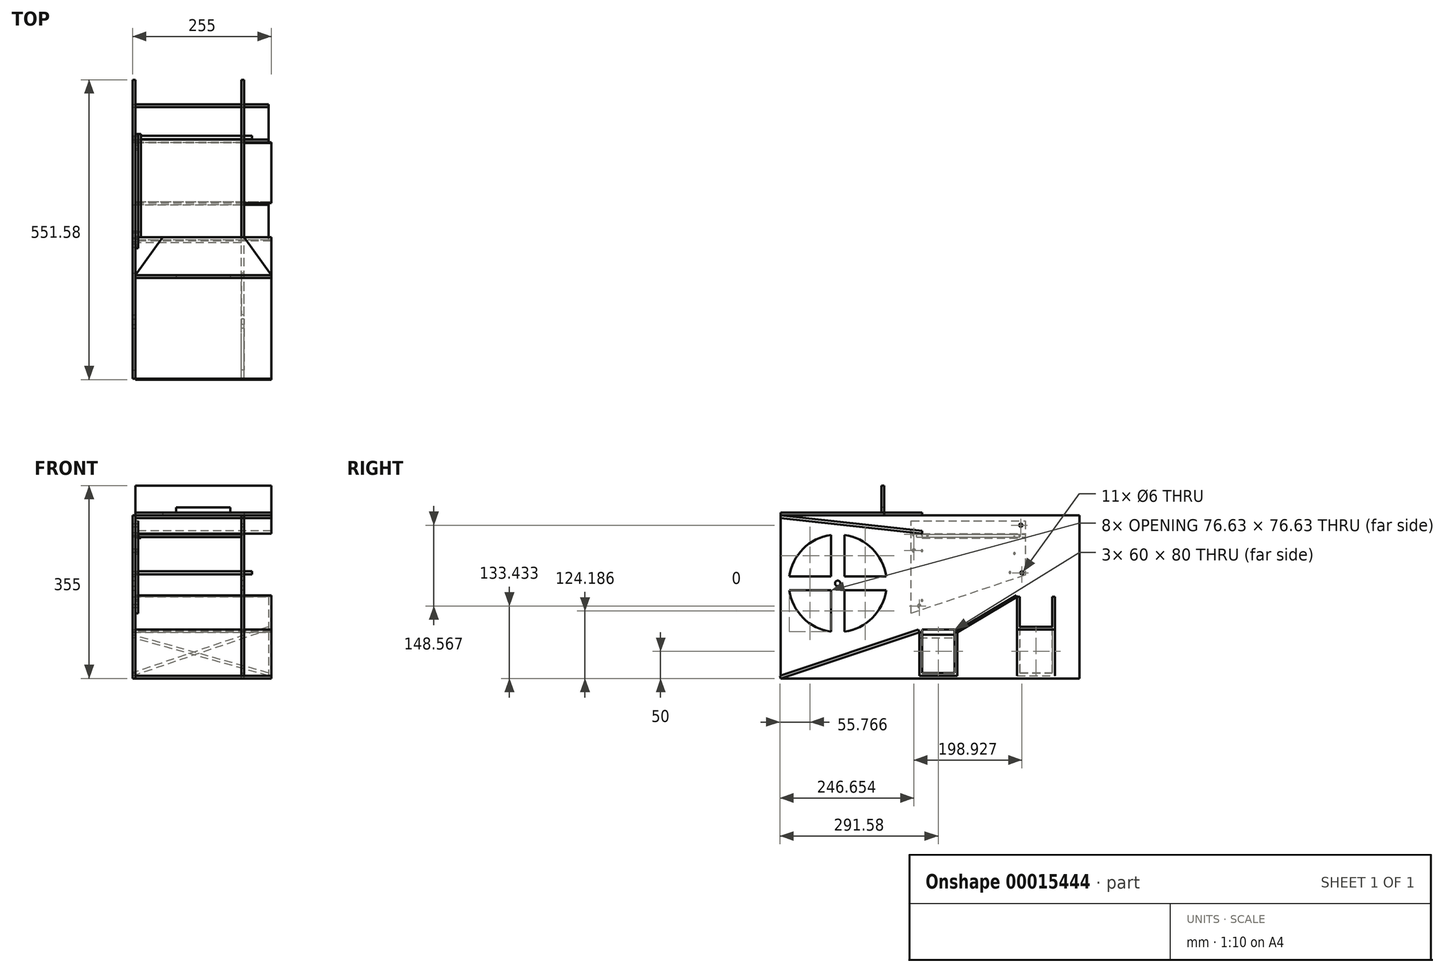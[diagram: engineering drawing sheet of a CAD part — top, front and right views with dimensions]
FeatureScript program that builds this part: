
annotation { "Feature Type Name" : "Feature", "Feature Type Description" : "" }
export const myFeature = defineFeature(function(context is Context, id is Id, definition is map)
    precondition{}
    {
        {
            var Q0;
            Q0=qCreatedBy(makeId("Right.planeOp"),FACE);
            var sketch = newSketch(context, id + "F0", { "sketchPlane" : qUnion([Q0])});
            skLineSegment(sketch, "E0.bottom", {"start": v(0, 0) * mm, "end": v(550, 0) * mm});
            skLineSegment(sketch, "E0.top", {"start": v(0, 300) * mm, "end": v(550, 300) * mm});
            skLineSegment(sketch, "E0.left", {"start": v(0, 0) * mm, "end": v(0, 300) * mm});
            skLineSegment(sketch, "E0.right", {"start": v(550, 0) * mm, "end": v(550, 300) * mm});
            skSolve(sketch);
        }
        {
            var Q0;
            Q0 = qSketchRegion(id + "F0", true);
            extrude(context, id + "F1", {"entities" : qUnion([Q0]), "depth" : 5 * mm});
        }
        {
            var Q0;
            Q0=makeQuery(id+"F1.opExtrude","CAP_FACE",FACE,{"disambiguationData":[OSD([sQuery(id+"F0.wireOp",EDGE,"E0.bottom"),sQuery(id+"F0.wireOp",EDGE,"E0.top"),sQuery(id+"F0.wireOp",EDGE,"E0.left"),sQuery(id+"F0.wireOp",EDGE,"E0.right")])],"isStart":false});
            var sketch = newSketch(context, id + "F2", { "sketchPlane" : qUnion([Q0])});
            skCircle(sketch, "E1", {"center": v(105, 175) * mm, "radius": 90 * mm});
            skLineSegment(sketch, "E2", {"start": v(52.33, 330.04) * mm, "end": v(82.37, 300) * mm});
            skLineSegment(sketch, "E3", {"start": v(82.37, 300) * mm, "end": v(199.7, 300) * mm});
            skLineSegment(sketch, "E4", {"start": v(199.7, 300) * mm, "end": v(229.74, 330.04) * mm});
            skLineSegment(sketch, "E5", {"start": v(82.37, 300) * mm, "end": v(250, 260) * mm});
            skLineSegment(sketch, "E6", {"start": v(250, 260) * mm, "end": v(440, 260) * mm});
            skLineSegment(sketch, "E7", {"start": v(440, 230) * mm, "end": v(250, 230) * mm});
            skLineSegment(sketch, "E8", {"start": v(440, 200) * mm, "end": v(256.2, 151.85) * mm});
            skLineSegment(sketch, "E9", {"start": v(263.12, 105.91) * mm, "end": v(44.4, 25.28) * mm});
            skLineSegment(sketch, "E10", {"start": v(440, 172.58) * mm, "end": v(440, 79.84) * mm});
            skLineSegment(sketch, "E11", {"start": v(440, 79.84) * mm, "end": v(500, 79.84) * mm});
            skLineSegment(sketch, "E12", {"start": v(500, 79.84) * mm, "end": v(500, 172.58) * mm});
            skLineSegment(sketch, "E13", {"start": v(323.12, 105.91) * mm, "end": v(323.12, 17.02) * mm});
            skLineSegment(sketch, "E14", {"start": v(323.12, 17.02) * mm, "end": v(263.12, 17.02) * mm});
            skLineSegment(sketch, "E15", {"start": v(263.12, 17.02) * mm, "end": v(263.12, 105.91) * mm});
            skLineSegment(sketch, "E16", {"start": v(323.12, 105.91) * mm, "end": v(440, 172.58) * mm});
            skSolve(sketch);
        }
        {
            var Q0;
            Q0=makeQuery(id+"F2.imprint","IMPRINT",FACE,{"disambiguationData":[TD([[makeQuery(id+"F2.imprint","IMPRINT",EDGE,{"derivedFrom":sQuery(id+"F2.wireOp",EDGE,"E1")}),-1.0]])]});
            var sketch = newSketch(context, id + "F3", { "sketchPlane" : qUnion([Q0])});
            skLineSegment(sketch, "E17", {"start": v(240, 290) * mm, "end": v(450, 290) * mm});
            skLineSegment(sketch, "E18", {"start": v(450, 290) * mm, "end": v(450, 190) * mm});
            skLineSegment(sketch, "E19", {"start": v(450, 190) * mm, "end": v(240, 120) * mm});
            skLineSegment(sketch, "E20", {"start": v(240, 120) * mm, "end": v(240, 290) * mm});
            skCircle(sketch, "E21", {"center": v(430, 260) * mm, "radius": 1.6 * mm});
            skCircle(sketch, "E22", {"center": v(430, 230) * mm, "radius": 1.6 * mm});
            skCircle(sketch, "E23", {"center": v(422.04, 195) * mm, "radius": 1.6 * mm});
            skCircle(sketch, "E24", {"center": v(260.07, 143.36) * mm, "radius": 1.6 * mm});
            skCircle(sketch, "E25", {"center": v(260.07, 235) * mm, "radius": 1.6 * mm});
            skCircle(sketch, "E26", {"center": v(260.07, 265) * mm, "radius": 1.6 * mm});
            skSolve(sketch);
        }
        {
            var Q0;
            Q0 = qSketchRegion(id + "F3", true);
            extrude(context, id + "F4", {"entities" : qUnion([Q0]), "depth" : 5 * mm});
        }
        {
            var Q0;
            Q0=makeQuery(id+"F4.opExtrude","CAP_FACE",FACE,{"disambiguationData":[OSD([sQuery(id+"F3.wireOp",EDGE,"E17"),sQuery(id+"F3.wireOp",EDGE,"E18"),sQuery(id+"F3.wireOp",EDGE,"E19"),sQuery(id+"F3.wireOp",EDGE,"E20")])],"isStart":false});
            var sketch = newSketch(context, id + "F5", { "sketchPlane" : qUnion([Q0])});
            skLineSegment(sketch, "E27.0", {"start": v(250, 260) * mm, "end": v(440, 260) * mm});
            skLineSegment(sketch, "E28", {"start": v(250, 260) * mm, "end": v(250, 265) * mm});
            skLineSegment(sketch, "E29", {"start": v(250, 265) * mm, "end": v(440, 265) * mm});
            skLineSegment(sketch, "E30", {"start": v(440, 265) * mm, "end": v(440, 260) * mm});
            skSolve(sketch);
        }
        {
            var Q0;
            Q0 = qSketchRegion(id + "F5", true);
            extrude(context, id + "F6", {"entities" : qUnion([Q0]), "depth" : 190 * mm});
        }
        {
            var Q0;
            Q0=makeQuery(id+"F2.imprint","IMPRINT",FACE,{"disambiguationData":[TD([[makeQuery(id+"F2.imprint","IMPRINT",EDGE,{"derivedFrom":sQuery(id+"F2.wireOp",EDGE,"E1")}),-1.0]])]});
            var sketch = newSketch(context, id + "F7", { "sketchPlane" : qUnion([Q0])});
            skArc(sketch, "E31.0", {"start": v(117.5, 85.87) * mm, "mid": v(168.64, 111.36) * mm, "end": v(194.13, 162.5) * mm});
            skLineSegment(sketch, "E32.rect.bottom", {"start": v(117.5, 85.87) * mm, "end": v(92.5, 85.87) * mm, "construction": true});
            skLineSegment(sketch, "E32.rect.top", {"start": v(117.5, 264.13) * mm, "end": v(92.5, 264.13) * mm, "construction": true});
            skLineSegment(sketch, "E32.rect.left", {"start": v(117.5, 85.87) * mm, "end": v(117.5, 162.5) * mm});
            skLineSegment(sketch, "E32.rect.right", {"start": v(92.5, 85.87) * mm, "end": v(92.5, 162.5) * mm});
            skLineSegment(sketch, "E33.rect.bottom", {"start": v(15.87, 187.5) * mm, "end": v(92.5, 187.5) * mm});
            skLineSegment(sketch, "E33.rect.top", {"start": v(15.87, 162.5) * mm, "end": v(92.5, 162.5) * mm});
            skLineSegment(sketch, "E33.rect.left", {"start": v(15.87, 187.5) * mm, "end": v(15.87, 162.5) * mm, "construction": true});
            skLineSegment(sketch, "E33.rect.right", {"start": v(194.13, 187.5) * mm, "end": v(194.13, 162.5) * mm, "construction": true});
            skLineSegment(sketch, "E34.trimOffspring", {"start": v(92.5, 187.5) * mm, "end": v(92.5, 264.13) * mm});
            skLineSegment(sketch, "E35.trimOffspring", {"start": v(117.5, 187.5) * mm, "end": v(194.13, 187.5) * mm});
            skLineSegment(sketch, "E36.trimOffspring", {"start": v(117.5, 187.5) * mm, "end": v(117.5, 264.13) * mm});
            skLineSegment(sketch, "E37.trimOffspring", {"start": v(117.5, 162.5) * mm, "end": v(194.13, 162.5) * mm});
            skArc(sketch, "E38.trimOffspring", {"start": v(194.13, 187.5) * mm, "mid": v(168.64, 238.64) * mm, "end": v(117.5, 264.13) * mm});
            skArc(sketch, "E39.trimOffspring", {"start": v(92.5, 264.13) * mm, "mid": v(41.36, 238.64) * mm, "end": v(15.87, 187.5) * mm});
            skArc(sketch, "E40.trimOffspring", {"start": v(15.87, 162.5) * mm, "mid": v(41.36, 111.36) * mm, "end": v(92.5, 85.87) * mm});
            skCircle(sketch, "E41", {"center": v(105, 175) * mm, "radius": 5 * mm});
            skSolve(sketch);
        }
        {
            var Q0;
            Q0 = qSketchRegion(id + "F7", true);
            extrude(context, id + "F8", {"entities" : qUnion([Q0]), "operationType" : NewBodyOperationType.REMOVE, "endBound" : BoundingType.THROUGH_ALL, "oppositeDirection" : true, "depth" : 25 * mm});
        }
        {
            var Q0;
            Q0=makeQuery(id+"F4.opExtrude","SWEPT_FACE",FACE,{"disambiguationData":[OSD([sQuery(id+"F3.wireOp",EDGE,"E18")])]});
            var sketch = newSketch(context, id + "F9", { "sketchPlane" : qUnion([Q0])});
            skPoint(sketch, "E42.0", {"position": v(-10, 260) * mm});
            skLineSegment(sketch, "E43", {"start": v(-10, 260) * mm, "end": v(-10, 266.5) * mm});
            skLineSegment(sketch, "E44", {"start": v(-10, 266.5) * mm, "end": v(-15, 266.5) * mm});
            skLineSegment(sketch, "E45", {"start": v(-15, 266.5) * mm, "end": v(-15, 265) * mm});
            skLineSegment(sketch, "E46", {"start": v(-15, 265) * mm, "end": v(-11.5, 265) * mm});
            skLineSegment(sketch, "E47", {"start": v(-11.5, 265) * mm, "end": v(-11.5, 260) * mm});
            skLineSegment(sketch, "E48", {"start": v(-11.5, 260) * mm, "end": v(-15, 260) * mm});
            skLineSegment(sketch, "E49", {"start": v(-15, 260) * mm, "end": v(-15, 258.5) * mm});
            skLineSegment(sketch, "E50", {"start": v(-15, 258.5) * mm, "end": v(-10, 258.5) * mm});
            skLineSegment(sketch, "E51", {"start": v(-10, 258.5) * mm, "end": v(-10, 260) * mm});
            skSolve(sketch);
        }
        {
            var Q0;
            Q0 = qSketchRegion(id + "F9", true);
            var Q1;
            Q1=makeQuery(id+"F4.opExtrude","SWEPT_FACE",FACE,{"disambiguationData":[OSD([sQuery(id+"F3.wireOp",EDGE,"E20")])]});
            extrude(context, id + "F10", {"entities" : qUnion([Q0]), "oppositeDirection" : true, "endBoundEntityFace" : qUnion([Q1]), "depth" : 190 * mm});
        }
        {
            var Q0;
            Q0=makeQuery(id+"F6.opExtrude","CAP_FACE",FACE,{"disambiguationData":[OSD([sQuery(id+"F5.wireOp",EDGE,"E27.0"),sQuery(id+"F5.wireOp",EDGE,"E28"),sQuery(id+"F5.wireOp",EDGE,"E29"),sQuery(id+"F5.wireOp",EDGE,"E30")])],"isStart":false});
            var sketch = newSketch(context, id + "F11", { "sketchPlane" : qUnion([Q0])});
            skLineSegment(sketch, "E52.0", {"start": v(0, 300) * mm, "end": v(550, 300) * mm});
            skLineSegment(sketch, "E52.1", {"start": v(0, 0) * mm, "end": v(0, 300) * mm});
            skArc(sketch, "E52.2", {"start": v(92.5, 264.13) * mm, "mid": v(41.36, 238.64) * mm, "end": v(15.87, 187.5) * mm});
            skLineSegment(sketch, "E52.3", {"start": v(0, 0) * mm, "end": v(550, 0) * mm});
            skLineSegment(sketch, "E52.4", {"start": v(550, 0) * mm, "end": v(550, 300) * mm});
            skLineSegment(sketch, "E53.0", {"start": v(117.5, 187.5) * mm, "end": v(117.5, 264.13) * mm});
            skLineSegment(sketch, "E53.1", {"start": v(117.5, 187.5) * mm, "end": v(194.13, 187.5) * mm});
            skLineSegment(sketch, "E53.2", {"start": v(117.5, 162.5) * mm, "end": v(194.13, 162.5) * mm});
            skLineSegment(sketch, "E53.3", {"start": v(117.5, 85.87) * mm, "end": v(117.5, 162.5) * mm});
            skLineSegment(sketch, "E53.4", {"start": v(92.5, 85.87) * mm, "end": v(92.5, 162.5) * mm});
            skLineSegment(sketch, "E53.5", {"start": v(15.87, 162.5) * mm, "end": v(92.5, 162.5) * mm});
            skLineSegment(sketch, "E53.6", {"start": v(15.87, 187.5) * mm, "end": v(92.5, 187.5) * mm});
            skLineSegment(sketch, "E53.7", {"start": v(92.5, 187.5) * mm, "end": v(92.5, 264.13) * mm});
            skCircle(sketch, "E53.8", {"center": v(105, 175) * mm, "radius": 5 * mm});
            skArc(sketch, "E54.trimOffspring", {"start": v(194.13, 187.5) * mm, "mid": v(168.64, 238.64) * mm, "end": v(117.5, 264.13) * mm});
            skArc(sketch, "E55.trimOffspring", {"start": v(15.87, 162.5) * mm, "mid": v(41.36, 111.36) * mm, "end": v(92.5, 85.87) * mm});
            skArc(sketch, "E56.trimOffspring", {"start": v(117.5, 85.87) * mm, "mid": v(168.64, 111.36) * mm, "end": v(194.13, 162.5) * mm});
            skSolve(sketch);
        }
        {
            var Q0;
            Q0 = qSketchRegion(id + "F11", true);
            extrude(context, id + "F12", {"entities" : qUnion([Q0]), "depth" : 5 * mm});
        }
        {
            var Q0;
            Q0=makeQuery(id+"F2.imprint","IMPRINT",FACE,{"disambiguationData":[TD([[makeQuery(id+"F2.imprint","IMPRINT",EDGE,{"derivedFrom":sQuery(id+"F2.wireOp",EDGE,"E1")}),-1.0]])]});
            var sketch = newSketch(context, id + "F13", { "sketchPlane" : qUnion([Q0])});
            skLineSegment(sketch, "E57.bottom", {"start": v(440, 10) * mm, "end": v(500, 10) * mm});
            skLineSegment(sketch, "E57.top", {"start": v(440, 90) * mm, "end": v(500, 90) * mm});
            skLineSegment(sketch, "E57.left", {"start": v(440, 10) * mm, "end": v(440, 90) * mm});
            skLineSegment(sketch, "E57.right", {"start": v(500, 10) * mm, "end": v(500, 90) * mm});
            skLineSegment(sketch, "E58.0", {"start": v(550, 0) * mm, "end": v(550, 300) * mm, "construction": true});
            skSolve(sketch);
        }
        {
            var Q0;
            Q0 = qSketchRegion(id + "F13", true);
            extrude(context, id + "F14", {"entities" : qUnion([Q0]), "operationType" : NewBodyOperationType.REMOVE, "endBound" : BoundingType.THROUGH_ALL, "oppositeDirection" : true, "depth" : 25 * mm});
        }
        {
            var Q0;
            Q0=makeQuery(id+"F12.opExtrude","CAP_FACE",FACE,{"disambiguationData":[OSD([sQuery(id+"F11.wireOp",EDGE,"E52.0"),sQuery(id+"F11.wireOp",EDGE,"E52.1"),sQuery(id+"F11.wireOp",EDGE,"E52.2"),sQuery(id+"F11.wireOp",EDGE,"E52.3"),sQuery(id+"F11.wireOp",EDGE,"E52.4"),sQuery(id+"F11.wireOp",EDGE,"E53.0"),sQuery(id+"F11.wireOp",EDGE,"E53.1"),sQuery(id+"F11.wireOp",EDGE,"E53.2"),sQuery(id+"F11.wireOp",EDGE,"E53.3"),sQuery(id+"F11.wireOp",EDGE,"E53.4"),sQuery(id+"F11.wireOp",EDGE,"E53.5"),sQuery(id+"F11.wireOp",EDGE,"E53.6"),sQuery(id+"F11.wireOp",EDGE,"E53.7"),sQuery(id+"F11.wireOp",EDGE,"E53.8"),sQuery(id+"F11.wireOp",EDGE,"E54.trimOffspring"),sQuery(id+"F11.wireOp",EDGE,"E55.trimOffspring"),sQuery(id+"F11.wireOp",EDGE,"E56.trimOffspring")])],"isStart":false});
            var sketch = newSketch(context, id + "F15", { "sketchPlane" : qUnion([Q0])});
            skLineSegment(sketch, "E59.bottom", {"start": v(260, 10) * mm, "end": v(320, 10) * mm});
            skLineSegment(sketch, "E59.top", {"start": v(260, 90) * mm, "end": v(320, 90) * mm});
            skLineSegment(sketch, "E59.left", {"start": v(260, 10) * mm, "end": v(260, 90) * mm});
            skLineSegment(sketch, "E59.right", {"start": v(320, 10) * mm, "end": v(320, 90) * mm});
            skSolve(sketch);
        }
        {
            var Q0;
            Q0 = qSketchRegion(id + "F15", true);
            extrude(context, id + "F16", {"entities" : qUnion([Q0]), "operationType" : NewBodyOperationType.REMOVE, "endBound" : BoundingType.THROUGH_ALL, "oppositeDirection" : true, "depth" : 25 * mm});
        }
        {
            var Q0;
            Q0=qCreatedBy(makeId("Right.planeOp"),FACE);
            var sketch = newSketch(context, id + "F17", { "sketchPlane" : qUnion([Q0])});
            skLineSegment(sketch, "E60.0", {"start": v(440, 10) * mm, "end": v(440, 90) * mm, "construction": true});
            skLineSegment(sketch, "E61.0", {"start": v(500, 10) * mm, "end": v(500, 90) * mm, "construction": true});
            skLineSegment(sketch, "E62.0", {"start": v(440, 10) * mm, "end": v(500, 10) * mm, "construction": true});
            skLineSegment(sketch, "E63.0", {"start": v(435, 5) * mm, "end": v(435, 150) * mm});
            skLineSegment(sketch, "E63.2", {"start": v(435, 5) * mm, "end": v(505, 5) * mm});
            skLineSegment(sketch, "E63.4", {"start": v(505, 150) * mm, "end": v(505, 5) * mm});
            skLineSegment(sketch, "E64", {"start": v(435, 150) * mm, "end": v(505, 150) * mm});
            skSolve(sketch);
        }
        {
            var Q0;
            Q0=qCreatedBy(makeId("Right.planeOp"),FACE);
            cPlane(context, id + "F18", {"entities" : qUnion([Q0]), "cplaneType" : CPlaneType.OFFSET, "offset" : 250 * mm, "width" : 150 * mm, "height" : 150 * mm});
        }
        {
            var Q0;
            Q0=qCreatedBy(id+"F18.planeOp",FACE);
            var sketch = newSketch(context, id + "F19", { "sketchPlane" : qUnion([Q0])});
            skLineSegment(sketch, "E65.0.3", {"start": v(505, 150) * mm, "end": v(435, 150) * mm});
            skLineSegment(sketch, "E66", {"start": v(435, 150) * mm, "end": v(435, 90) * mm});
            skLineSegment(sketch, "E67", {"start": v(435, 90) * mm, "end": v(505, 90) * mm});
            skLineSegment(sketch, "E68", {"start": v(505, 90) * mm, "end": v(505, 150) * mm});
            skSolve(sketch);
        }
        {
            var Q1;
            Q1 = qSketchRegion(id + "F17", true);
            var Q2;
            Q2 = qSketchRegion(id + "F19", true);
            loft(context, id + "F20", {"sheetProfilesArray" : [{ "sheetProfileEntities" : qUnion([Q1]) }, { "sheetProfileEntities" : qUnion([Q2]) }]});
        }
        {
            var Q0;
            Q0=makeQuery(id+"F20.opLoft","SWEPT_FACE",FACE,{"disambiguationData":[OSD([sQuery(id+"F17.wireOp",EDGE,"E63.0"),sQuery(id+"F17.wireOp",EDGE,"E63.4"),sQuery(id+"F17.wireOp",EDGE,"E64"),sQuery(id+"F19.wireOp",EDGE,"E65.0.3"),sQuery(id+"F19.wireOp",EDGE,"E66"),sQuery(id+"F19.wireOp",EDGE,"E68")])]});
            var Q1;
            Q1=makeQuery(id+"F20.opLoft","CAP_FACE",FACE,{"disambiguationData":[OSD([makeQuery(id+"F19.imprint","IMPRINT",FACE,{"disambiguationData":[TD([[makeQuery(id+"F19.imprint","IMPRINT",EDGE,{"derivedFrom":sQuery(id+"F19.wireOp",EDGE,"E65.0.3")}),1.0]])]})])],"isStart":true});
            var Q2;
            Q2=makeQuery(id+"F20.opLoft","CAP_FACE",FACE,{"disambiguationData":[OSD([makeQuery(id+"F17.imprint","IMPRINT",FACE,{"disambiguationData":[TD([[makeQuery(id+"F17.imprint","IMPRINT",EDGE,{"derivedFrom":sQuery(id+"F17.wireOp",EDGE,"E63.0")}),-1.0]])]})])],"isStart":true});
            shell(context, id + "F21", {"entities" : qUnion([Q0, Q1, Q2]), "thickness" : 5 * mm});
        }
        {
            var Q0;
            Q0=qCreatedBy(id+"F18.planeOp",FACE);
            var sketch = newSketch(context, id + "F22", { "sketchPlane" : qUnion([Q0])});
            skLineSegment(sketch, "E69.bottom", {"start": v(255, 85) * mm, "end": v(325, 85) * mm});
            skLineSegment(sketch, "E69.top", {"start": v(255, 5) * mm, "end": v(325, 5) * mm});
            skLineSegment(sketch, "E69.left", {"start": v(255, 85) * mm, "end": v(255, 5) * mm});
            skLineSegment(sketch, "E69.right", {"start": v(325, 85) * mm, "end": v(325, 5) * mm});
            skPoint(sketch, "E70.0", {"position": v(260, 10) * mm});
            skPoint(sketch, "E70.1", {"position": v(320, 10) * mm});
            skSolve(sketch);
        }
        {
            var Q0;
            Q0=qCreatedBy(makeId("Right.planeOp"),FACE);
            var sketch = newSketch(context, id + "F23", { "sketchPlane" : qUnion([Q0])});
            skPoint(sketch, "E71.0", {"position": v(255, 85) * mm});
            skLineSegment(sketch, "E71.1", {"start": v(255, 85) * mm, "end": v(325, 85) * mm});
            skPoint(sketch, "E71.2", {"position": v(325, 85) * mm});
            skLineSegment(sketch, "E72", {"start": v(255, 85) * mm, "end": v(255, 75) * mm});
            skLineSegment(sketch, "E73", {"start": v(255, 75) * mm, "end": v(325, 75) * mm});
            skLineSegment(sketch, "E74", {"start": v(325, 75) * mm, "end": v(325, 85) * mm});
            skSolve(sketch);
        }
        {
            var Q0;
            Q0 = qSketchRegion(id + "F22", true);
            var Q1;
            Q1 = qSketchRegion(id + "F23", true);
            loft(context, id + "F24", {"sheetProfilesArray" : [{ "sheetProfileEntities" : qUnion([Q0]) }, { "sheetProfileEntities" : qUnion([Q1]) }]});
        }
        {
            var Q0;
            Q0=makeQuery(id+"F24.opLoft","SWEPT_FACE",FACE,{"disambiguationData":[OSD([sQuery(id+"F22.wireOp",EDGE,"E69.bottom"),sQuery(id+"F22.wireOp",EDGE,"E69.left"),sQuery(id+"F22.wireOp",EDGE,"E69.right"),sQuery(id+"F23.wireOp",EDGE,"E71.1"),sQuery(id+"F23.wireOp",EDGE,"a4f3d3e9-b016-48f9-8659-834d968ab62a"),sQuery(id+"F23.wireOp",EDGE,"384a152d-da16-4bd5-ac45-8ecb57b86d58")])]});
            var Q1;
            Q1=makeQuery(id+"F24.opLoft","CAP_FACE",FACE,{"disambiguationData":[OSD([makeQuery(id+"F22.imprint","IMPRINT",FACE,{"disambiguationData":[TD([[makeQuery(id+"F22.imprint","IMPRINT",EDGE,{"derivedFrom":sQuery(id+"F22.wireOp",EDGE,"E69.bottom")}),-1.0]])]})])],"isStart":true});
            var Q2;
            Q2=makeQuery(id+"F24.opLoft","CAP_FACE",FACE,{"disambiguationData":[OSD([makeQuery(id+"F23.imprint","IMPRINT",FACE,{"disambiguationData":[TD([[makeQuery(id+"F23.imprint","IMPRINT",EDGE,{"derivedFrom":sQuery(id+"F23.wireOp",EDGE,"E71.1")}),-1.0]])]})])],"isStart":true});
            shell(context, id + "F25", {"entities" : qUnion([Q0, Q1, Q2]), "thickness" : 5 * mm});
        }
        {
            var Q0;
            Q0=makeQuery(id+"F1.opExtrude","CAP_FACE",FACE,{"disambiguationData":[OSD([sQuery(id+"F0.wireOp",EDGE,"E0.bottom"),sQuery(id+"F0.wireOp",EDGE,"E0.top"),sQuery(id+"F0.wireOp",EDGE,"E0.left"),sQuery(id+"F0.wireOp",EDGE,"E0.right")])],"isStart":false});
            var sketch = newSketch(context, id + "F26", { "sketchPlane" : qUnion([Q0])});
            skPoint(sketch, "E75.0", {"position": v(435, 150) * mm});
            skPoint(sketch, "E76.0", {"position": v(325, 85) * mm});
            skLineSegment(sketch, "E77", {"start": v(325, 85) * mm, "end": v(435, 150) * mm});
            skLineSegment(sketch, "E78", {"start": v(435, 150) * mm, "end": v(433.47, 152.58) * mm});
            skLineSegment(sketch, "E79", {"start": v(433.47, 152.58) * mm, "end": v(323.47, 87.58) * mm});
            skLineSegment(sketch, "E80", {"start": v(323.47, 87.58) * mm, "end": v(325, 85) * mm});
            skSolve(sketch);
        }
        {
            var Q0;
            Q0 = qSketchRegion(id + "F26", true);
            extrude(context, id + "F27", {"entities" : qUnion([Q0]), "depth" : 250 * mm});
        }
        {
            var Q0;
            Q0=makeQuery(id+"F10.opExtrude","SWEPT_FACE",FACE,{"disambiguationData":[OSD([sQuery(id+"F9.wireOp",EDGE,"E47")])]});
            var sketch = newSketch(context, id + "F28", { "sketchPlane" : qUnion([Q0])});
            skCircle(sketch, "E81", {"center": v(440, 262.5) * mm, "radius": 1.6 * mm});
            skCircle(sketch, "E82", {"center": v(270, 262.5) * mm, "radius": 1.6 * mm});
            skLineSegment(sketch, "E83.0", {"start": v(450, 265) * mm, "end": v(450, 260) * mm, "construction": true});
            skPoint(sketch, "E84", {"position": v(450, 262.5) * mm});
            skSolve(sketch);
        }
        {
            var Q0;
            Q0 = qSketchRegion(id + "F28", true);
            extrude(context, id + "F29", {"entities" : qUnion([Q0]), "operationType" : NewBodyOperationType.REMOVE, "endBound" : BoundingType.THROUGH_ALL, "oppositeDirection" : true, "depth" : 25 * mm});
        }
        {
            var Q0;
            Q0=makeQuery(id+"F1.opExtrude","CAP_FACE",FACE,{"disambiguationData":[OSD([sQuery(id+"F0.wireOp",EDGE,"E0.bottom"),sQuery(id+"F0.wireOp",EDGE,"E0.top"),sQuery(id+"F0.wireOp",EDGE,"E0.left"),sQuery(id+"F0.wireOp",EDGE,"E0.right")])],"isStart":false});
            var sketch = newSketch(context, id + "F30", { "sketchPlane" : qUnion([Q0])});
            skPoint(sketch, "E85.0", {"position": v(260, 266.5) * mm});
            skLineSegment(sketch, "E86", {"start": v(260, 266.5) * mm, "end": v(0, 294.97) * mm});
            skLineSegment(sketch, "E87", {"start": v(0, 294.97) * mm, "end": v(0, 300) * mm});
            skLineSegment(sketch, "E88", {"start": v(0, 300) * mm, "end": v(260.54, 271.47) * mm});
            skLineSegment(sketch, "E89", {"start": v(260.54, 271.47) * mm, "end": v(260, 266.5) * mm});
            skSolve(sketch);
        }
        {
            var Q0;
            Q0 = qSketchRegion(id + "F30", true);
            extrude(context, id + "F31", {"entities" : qUnion([Q0]), "depth" : 250 * mm});
        }
        {
            var Q0;
            Q0=makeQuery(id+"F1.opExtrude","CAP_FACE",FACE,{"disambiguationData":[OSD([sQuery(id+"F0.wireOp",EDGE,"E0.bottom"),sQuery(id+"F0.wireOp",EDGE,"E0.top"),sQuery(id+"F0.wireOp",EDGE,"E0.left"),sQuery(id+"F0.wireOp",EDGE,"E0.right")])],"isStart":false});
            var sketch = newSketch(context, id + "F32", { "sketchPlane" : qUnion([Q0])});
            skLineSegment(sketch, "E90", {"start": v(0, 0) * mm, "end": v(255, 85) * mm});
            skLineSegment(sketch, "E91", {"start": v(255, 85) * mm, "end": v(253.42, 89.74) * mm});
            skLineSegment(sketch, "E92", {"start": v(253.42, 89.74) * mm, "end": v(-1.58, 4.74) * mm});
            skLineSegment(sketch, "E93", {"start": v(-1.58, 4.74) * mm, "end": v(0, 0) * mm});
            skPoint(sketch, "E94.0", {"position": v(255, 85) * mm});
            skSolve(sketch);
        }
        {
            var Q0;
            Q0 = qSketchRegion(id + "F32", true);
            extrude(context, id + "F33", {"entities" : qUnion([Q0]), "depth" : 250 * mm});
        }
        {
            var Q0;
            Q0=makeQuery(id+"F1.opExtrude","SWEPT_FACE",FACE,{"disambiguationData":[OSD([sQuery(id+"F0.wireOp",EDGE,"E0.top")])]});
            var sketch = newSketch(context, id + "F34", { "sketchPlane" : qUnion([Q0])});
            skLineSegment(sketch, "E95.0.0", {"start": v(5, 260.54) * mm, "end": v(5, 0) * mm, "construction": true});
            skLineSegment(sketch, "E95.0.1", {"start": v(5, 0) * mm, "end": v(255, 0) * mm});
            skLineSegment(sketch, "E95.0.2", {"start": v(255, 0) * mm, "end": v(255, 260.54) * mm, "construction": true});
            skLineSegment(sketch, "E95.0.3", {"start": v(255, 260.54) * mm, "end": v(5, 260.54) * mm, "construction": true});
            skLineSegment(sketch, "E96", {"start": v(5, 0) * mm, "end": v(5, 190.54) * mm});
            skLineSegment(sketch, "E97", {"start": v(5, 190.54) * mm, "end": v(55, 260.54) * mm});
            skLineSegment(sketch, "E98", {"start": v(55, 260.54) * mm, "end": v(205, 260.54) * mm});
            skLineSegment(sketch, "E99", {"start": v(205, 260.54) * mm, "end": v(255, 190.54) * mm});
            skLineSegment(sketch, "E100", {"start": v(255, 190.54) * mm, "end": v(255, 0) * mm});
            skSolve(sketch);
        }
        {
            var Q0;
            Q0 = qSketchRegion(id + "F34", true);
            extrude(context, id + "F35", {"entities" : qUnion([Q0]), "depth" : 5 * mm});
        }
        {
            var Q0;
            Q0=makeQuery(id+"F35.opExtrude","CAP_FACE",FACE,{"disambiguationData":[OSD([sQuery(id+"F34.wireOp",EDGE,"E95.0.1"),sQuery(id+"F34.wireOp",EDGE,"E96"),sQuery(id+"F34.wireOp",EDGE,"E97"),sQuery(id+"F34.wireOp",EDGE,"E98"),sQuery(id+"F34.wireOp",EDGE,"E99"),sQuery(id+"F34.wireOp",EDGE,"E100")])],"isStart":false});
            var sketch = newSketch(context, id + "F36", { "sketchPlane" : qUnion([Q0])});
            skLineSegment(sketch, "E101.bottom", {"start": v(5, 190.54) * mm, "end": v(255, 190.54) * mm});
            skLineSegment(sketch, "E101.top", {"start": v(5, 185.54) * mm, "end": v(255, 185.54) * mm});
            skLineSegment(sketch, "E101.left", {"start": v(5, 190.54) * mm, "end": v(5, 185.54) * mm});
            skLineSegment(sketch, "E101.right", {"start": v(255, 190.54) * mm, "end": v(255, 185.54) * mm});
            skSolve(sketch);
        }
        {
            var Q0;
            Q0 = qSketchRegion(id + "F36", true);
            extrude(context, id + "F37", {"entities" : qUnion([Q0]), "depth" : 50 * mm});
        }
        {
            var Q0;
            Q0=makeQuery(id+"F37.opExtrude","SWEPT_FACE",FACE,{"disambiguationData":[OSD([sQuery(id+"F36.wireOp",EDGE,"E101.top")])]});
            var sketch = newSketch(context, id + "F38", { "sketchPlane" : qUnion([Q0])});
            skLineSegment(sketch, "E102.bottom", {"start": v(80, 305) * mm, "end": v(180, 305) * mm});
            skLineSegment(sketch, "E102.top", {"start": v(80, 315) * mm, "end": v(180, 315) * mm});
            skLineSegment(sketch, "E102.left", {"start": v(80, 305) * mm, "end": v(80, 315) * mm});
            skLineSegment(sketch, "E102.right", {"start": v(180, 305) * mm, "end": v(180, 315) * mm});
            skPoint(sketch, "E103", {"position": v(130, 305) * mm});
            skSolve(sketch);
        }
        {
            var Q0;
            Q0 = qSketchRegion(id + "F38", true);
            extrude(context, id + "F39", {"entities" : qUnion([Q0]), "operationType" : NewBodyOperationType.REMOVE, "endBound" : BoundingType.THROUGH_ALL, "oppositeDirection" : true, "depth" : 25 * mm});
        }
        {
            var Q0;
            Q0=makeQuery(id+"F4.opExtrude","CAP_FACE",FACE,{"disambiguationData":[OSD([sQuery(id+"F3.wireOp",EDGE,"E17"),sQuery(id+"F3.wireOp",EDGE,"E18"),sQuery(id+"F3.wireOp",EDGE,"E19"),sQuery(id+"F3.wireOp",EDGE,"E20"),sQuery(id+"F3.wireOp",EDGE,"E21"),sQuery(id+"F3.wireOp",EDGE,"E22"),sQuery(id+"F3.wireOp",EDGE,"E23"),sQuery(id+"F3.wireOp",EDGE,"E24"),sQuery(id+"F3.wireOp",EDGE,"E25"),sQuery(id+"F3.wireOp",EDGE,"E26")])],"isStart":false});
            var sketch = newSketch(context, id + "F40", { "sketchPlane" : qUnion([Q0])});
            skCircle(sketch, "E104", {"center": v(442, 282) * mm, "radius": 3 * mm});
            skSolve(sketch);
        }
        {
            var Q0;
            Q0 = qSketchRegion(id + "F40", true);
            extrude(context, id + "F41", {"entities" : qUnion([Q0]), "operationType" : NewBodyOperationType.REMOVE, "endBound" : BoundingType.THROUGH_ALL, "oppositeDirection" : true, "depth" : 25 * mm, "hasSecondDirection" : true, "secondDirectionBound" : BoundingType.THROUGH_ALL, "secondDirectionOppositeDirection" : false, "secondDirectionDepth" : 25 * mm});
        }
        {
            var Q0;
            Q0=makeQuery(id+"F4.opExtrude","CAP_FACE",FACE,{"disambiguationData":[OSD([sQuery(id+"F3.wireOp",EDGE,"E17"),sQuery(id+"F3.wireOp",EDGE,"E18"),sQuery(id+"F3.wireOp",EDGE,"E19"),sQuery(id+"F3.wireOp",EDGE,"E20"),sQuery(id+"F3.wireOp",EDGE,"E21"),sQuery(id+"F3.wireOp",EDGE,"E22"),sQuery(id+"F3.wireOp",EDGE,"E23"),sQuery(id+"F3.wireOp",EDGE,"E24"),sQuery(id+"F3.wireOp",EDGE,"E25"),sQuery(id+"F3.wireOp",EDGE,"E26")])],"isStart":false});
            var sketch = newSketch(context, id + "F42", { "sketchPlane" : qUnion([Q0])});
            skCircle(sketch, "E105", {"center": v(444, 194.32) * mm, "radius": 3 * mm});
            skCircle(sketch, "E106", {"center": v(245.08, 265.44) * mm, "radius": 3 * mm});
            skCircle(sketch, "E107", {"center": v(255, 133.43) * mm, "radius": 3 * mm});
            skPoint(sketch, "E108", {"position": v(260.07, 265) * mm});
            skPoint(sketch, "E109", {"position": v(430, 260) * mm});
            skLineSegment(sketch, "E110", {"start": v(430, 260) * mm, "end": v(241.9, 265.53) * mm, "construction": true});
            skLineSegment(sketch, "E111", {"start": v(422.04, 195) * mm, "end": v(260.07, 143.36) * mm, "construction": true});
            skLineSegment(sketch, "E112", {"start": v(430, 230) * mm, "end": v(260.07, 235) * mm, "construction": true});
            skCircle(sketch, "E113", {"center": v(245.07, 235.44) * mm, "radius": 3 * mm});
            skSolve(sketch);
        }
        {
            var Q0;
            Q0 = qSketchRegion(id + "F42", true);
            extrude(context, id + "F43", {"entities" : qUnion([Q0]), "operationType" : NewBodyOperationType.REMOVE, "endBound" : BoundingType.THROUGH_ALL, "oppositeDirection" : true, "depth" : 25 * mm});
        }
        {
            var Q0;
            Q0=makeQuery(id+"F1.opExtrude","CAP_FACE",FACE,{"disambiguationData":[OSD([sQuery(id+"F0.wireOp",EDGE,"E0.bottom"),sQuery(id+"F0.wireOp",EDGE,"E0.top"),sQuery(id+"F0.wireOp",EDGE,"E0.left"),sQuery(id+"F0.wireOp",EDGE,"E0.right")])],"isStart":false});
            var sketch = newSketch(context, id + "F44", { "sketchPlane" : qUnion([Q0])});
            skCircle(sketch, "E114.0", {"center": v(444, 194.32) * mm, "radius": 3 * mm});
            skSolve(sketch);
        }
        {
            var Q0;
            Q0 = qSketchRegion(id + "F44", true);
            extrude(context, id + "F45", {"entities" : qUnion([Q0]), "depth" : 215 * mm});
        }
    });
